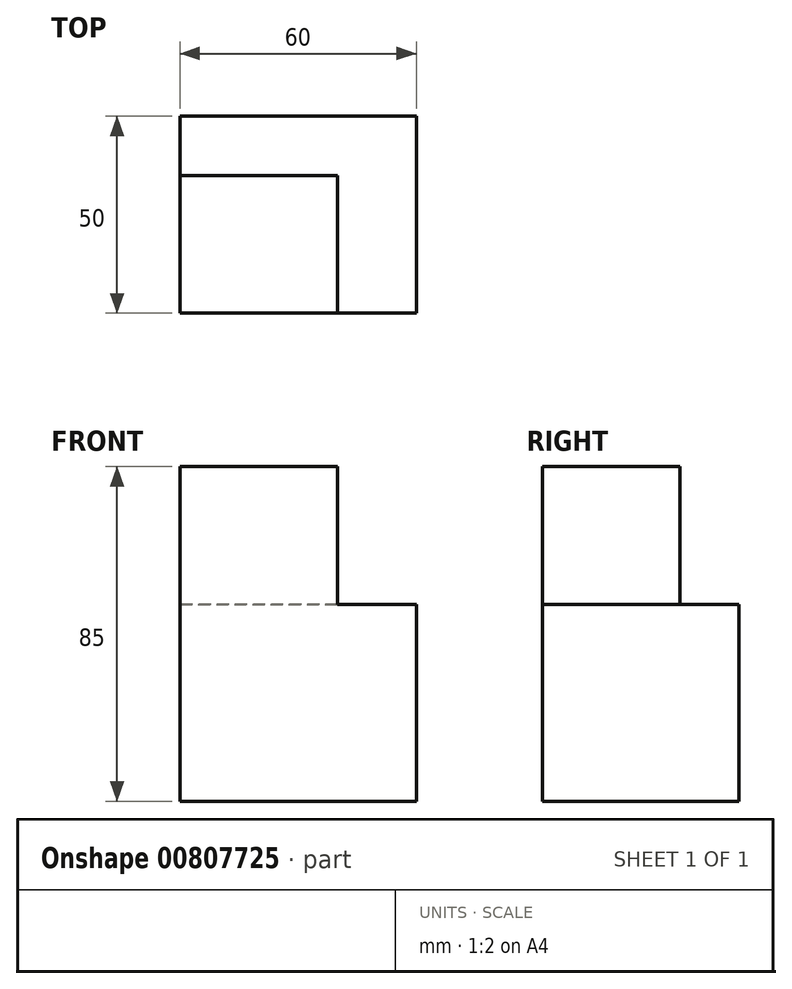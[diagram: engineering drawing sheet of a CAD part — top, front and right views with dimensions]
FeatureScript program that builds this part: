
annotation { "Feature Type Name" : "Feature", "Feature Type Description" : "" }
export const myFeature = defineFeature(function(context is Context, id is Id, definition is map)
    precondition{}
    {
        {
            var Q0;
            Q0=qCreatedBy(makeId("Top.planeOp"),FACE);
            cPlane(context, id + "F0", {"entities" : qUnion([Q0]), "cplaneType" : CPlaneType.OFFSET, "offset" : 50 * mm, "width" : 152.4 * mm, "height" : 152.4 * mm});
        }
        {
            var Q0;
            Q0=qCreatedBy(makeId("Top.planeOp"),FACE);
            var sketch = newSketch(context, id + "F1", { "sketchPlane" : qUnion([Q0])});
            skLineSegment(sketch, "E0.bottom", {"start": v(-30, 25) * mm, "end": v(30, 25) * mm});
            skLineSegment(sketch, "E0.top", {"start": v(-30, -25) * mm, "end": v(30, -25) * mm});
            skLineSegment(sketch, "E0.left", {"start": v(-30, 25) * mm, "end": v(-30, -25) * mm});
            skLineSegment(sketch, "E0.right", {"start": v(30, 25) * mm, "end": v(30, -25) * mm});
            skPoint(sketch, "E0.middle", {"position": v(0, 0) * mm});
            skLineSegment(sketch, "E1.bottom", {"start": v(-30, -25) * mm, "end": v(10, -25) * mm});
            skLineSegment(sketch, "E1.top", {"start": v(-30, 10) * mm, "end": v(10, 10) * mm});
            skLineSegment(sketch, "E1.left", {"start": v(-30, -25) * mm, "end": v(-30, 10) * mm});
            skLineSegment(sketch, "E1.right", {"start": v(10, -25) * mm, "end": v(10, 10) * mm});
            skSolve(sketch);
        }
        {
            var Q0;
            Q0=qCreatedBy(id+"F0.planeOp",FACE);
            var sketch = newSketch(context, id + "F2", { "sketchPlane" : qUnion([Q0])});
            skLineSegment(sketch, "E2.0.0", {"start": v(-30, 10) * mm, "end": v(-30, -25) * mm});
            skLineSegment(sketch, "E2.0.1", {"start": v(-30, -25) * mm, "end": v(10, -25) * mm});
            skLineSegment(sketch, "E2.0.2", {"start": v(10, -25) * mm, "end": v(10, 10) * mm});
            skLineSegment(sketch, "E2.0.3", {"start": v(10, 10) * mm, "end": v(-30, 10) * mm});
            skSolve(sketch);
        }
        {
            var Q0;
            {var subQ4=sQuery(id+"F1.wireOp",EDGE,"E1.top");Q0=makeQuery(id+"F1.imprint","IMPRINT",FACE,{"disambiguationData":[TD([[makeQuery(id+"F1.imprint","IMPRINT",EDGE,{"derivedFrom":subQ4}),-1.0]])]});}
            var Q1;
            {var subQ1=sQuery(id+"F1.wireOp",EDGE,"E0.bottom");Q1=makeQuery(id+"F1.imprint","IMPRINT",FACE,{"disambiguationData":[TD([[makeQuery(id+"F1.imprint","IMPRINT",EDGE,{"derivedFrom":subQ1}),-1.0]])]});}
            extrude(context, id + "F3", {"entities" : qUnion([Q0, Q1]), "depth" : 50 * mm, "offsetDistance" : 25 * mm});
        }
        {
            var Q0;
            Q0=makeQuery(id+"F2.imprint","IMPRINT",FACE,{"disambiguationData":[TD([[makeQuery(id+"F2.imprint","IMPRINT",EDGE,{"derivedFrom":sQuery(id+"F2.wireOp",EDGE,"E2.0.0")}),1.0]])]});
            extrude(context, id + "F4", {"entities" : qUnion([Q0]), "operationType" : NewBodyOperationType.ADD, "depth" : 35 * mm, "offsetDistance" : 25 * mm});
        }
    });
